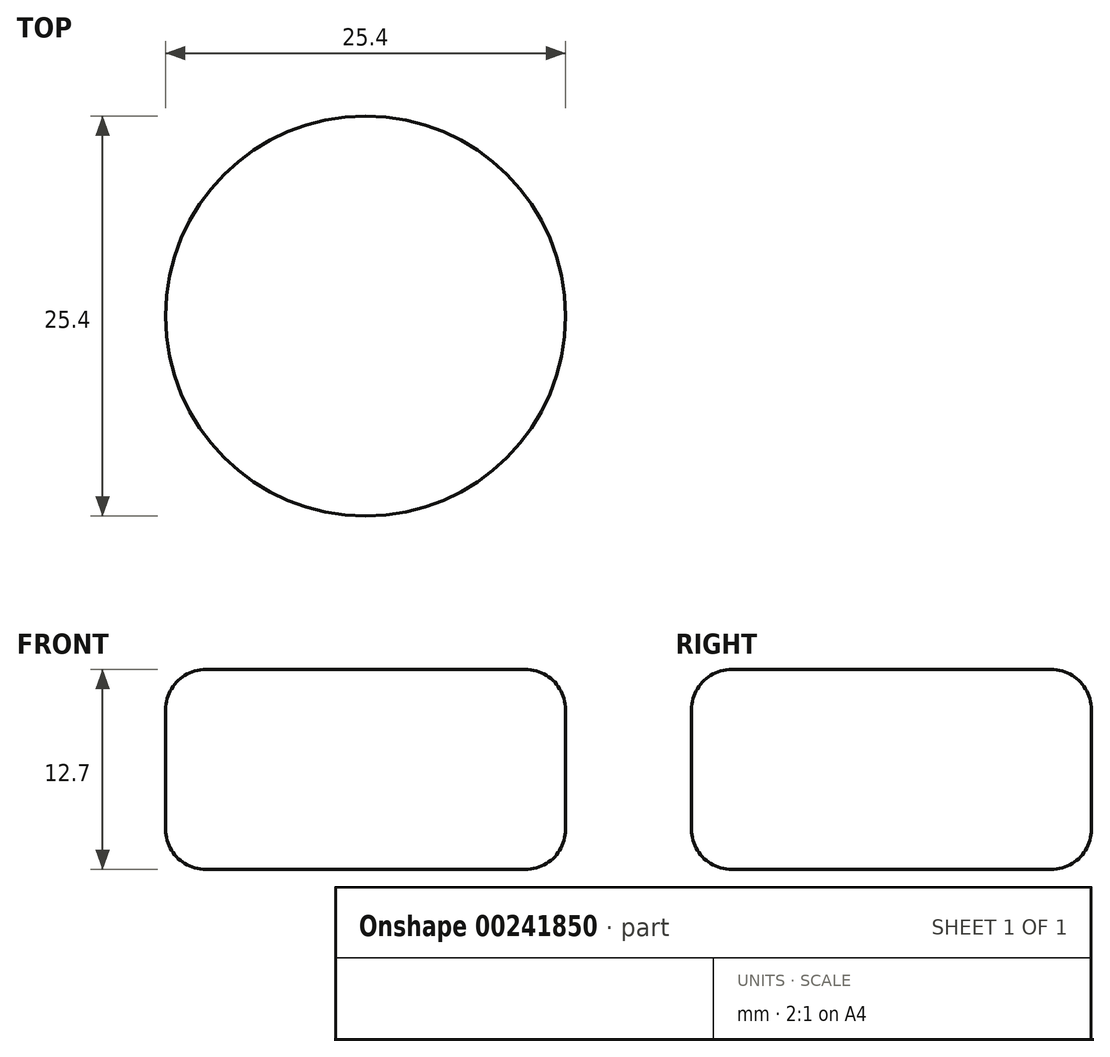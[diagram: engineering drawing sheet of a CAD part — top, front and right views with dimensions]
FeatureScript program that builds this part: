
annotation { "Feature Type Name" : "Feature", "Feature Type Description" : "" }
export const myFeature = defineFeature(function(context is Context, id is Id, definition is map)
    precondition{}
    {
        {
            var Q0;
            Q0=qCreatedBy(makeId("Top.planeOp"),FACE);
            var sketch = newSketch(context, id + "F0", { "sketchPlane" : qUnion([Q0])});
            skCircle(sketch, "E0", {"center": v(0, 0) * mm, "radius": 12.7 * mm});
            skSolve(sketch);
        }
        {
            var Q0;
            Q0 = qSketchRegion(id + "F0", true);
            extrude(context, id + "F1", {"entities" : qUnion([Q0]), "depth" : 12.7 * mm});
        }
        {
            var Q0;
            Q0=makeQuery(id+"F1.opExtrude","SWEPT_FACE",FACE,{"disambiguationData":[OSD([sQuery(id+"F0.wireOp",EDGE,"E0")])]});
            fillet(context, id + "F2", {"entities" : qUnion([Q0]), "radius" : 2.54 * mm, "tangentPropagation" : true, "allowEdgeOverflow" : false});
        }
    });
